# Revit family: Gleitlager T HV1, o.D., Ø20 bis Ø60mm (h=99mm bis 125mm)
name_source: partatom
category: HLS-Bauteile
revit_build: Autodesk Revit 2018 (Build: 20190510_1515(x64)
units: mm (PartAtom-declared; Revit-internal decimal feet)

## family parameters
Arbeitsebenenbasiert = Ja
Beim Laden mit Abzugskörper schneiden = Nein
Bemaßung runder Anschluss = Durchmesser verwenden
Gemeinsam genutzt = Ja
Immer vertikal = Nein
Klassifizierung = Keine
Raumberechnungspunkt = Nein
Teiletyp = Normal

## types (9) — shared parameters
Anzahl Rohrschellen = 2
Breite Schellenband = 35 mm
Breite Unterbau = 100 mm
Fabrikat = MEFA
Hersteller = MEFA
Kurztext1 = Gleitlager T 2 RS HV1 35x4
Länge Unterbau = 250 mm
Mengeneinheit = St
Schalldämmeinlage = ohne Dämmung
Sicherheitsfaktor = 1.54
Stärke Material = 8 mm  [stored 0.0262467 ft]
Stärke Schellenband = 4 mm
Verschluss = Mutter / Verschluss-Schraube
Vorgabe-Ansicht = 1219 mm
max. Höhe Unterbau = 125 mm
min. Höhe Unterbau = 100 mm
vpe = 1
zero-valued in all types: Dämmstärke

## per-type parameters (varying)
| type | Artikelnummer | EAN | Gewicht | Gewicht pro Bauteil | Kurztext2 | Schellenteil | max. Rohrachse | max. Rohraußendurchmesser | min. Rohrachse | min. Rohraußendurchmesser |
| Typ HV1, m. 2 RS, o.D., Ø20-22mm (h=99 bis 125mm) | 141afba0022 | 4250928460257 | 3.78 kg | 3.78 kg | 20 - 22 mm o. Dämm. 100x250 mm fsv | TL-141S_b0022 bis 0062, o.D : mit RS Ø20-22mm o.D | 136 mm | 22 mm  [stored 0.0721785 ft] | 109 mm | 20 mm  [stored 0.0656168 ft] |
| Typ HV1, m. 2 RS, o.D., Ø25mm (h=99 bis 125mm) | 141afba0025 | 4250928460264 | 3.80 kg | 3.80 kg | 25 mm o. Dämm. 100x250 mm fsv | TL-141S_b0022 bis 0062, o.D : mit RS Ø25mm o.D | 138 mm | 0 mm  [stored 0 ft] | 112 mm | 0 mm  [stored 0 ft] |
| Typ HV1, m. 2 RS, o.D., Ø27-28mm (h=99 bis 125mm) | 141afba0028 | 4250928460271 | 3.84 kg | 3.84 kg | 27 - 28 mm o. Dämm. 100x250 mm fsv | TL-141S_b0022 bis 0062, o.D : mit RS Ø27-28mm, o.D | 139 mm | 28 mm  [stored 0.0918635 ft] | 113 mm | 27 mm  [stored 0.0885827 ft] |
| Typ HV1, m. 2 RS, o.D., Ø32mm (h=99 bis 125mm) | 141afba0032 | 4250928460288 | 3.87 kg | 3.87 kg | 32 mm o. Dämm. 100x250 mm fsv | TL-141S_b0022 bis 0062, o.D : mit RS Ø32mm o.D | 141 mm | 0 mm  [stored 0 ft] | 115 mm | 0 mm  [stored 0 ft] |
| Typ HV1, m. 2 RS, o.D., Ø33-35mm (h=99 bis 125mm) | 141afba0035 | 4250928460295 | 3.89 kg | 3.89 kg | 33 - 35 mm o. Dämm. 100x250 mm fsv | TL-141S_b0022 bis 0062, o.D : mit RS Ø33-35mm o.D | 143 mm | 35 mm  [stored 0.114829 ft] | 116 mm | 33 mm |
| Typ HV1, m. 2 RS, o.D., Ø40-42mm (h=99 bis 125mm) | 141afba0042 | 4250928460301 | 3.95 kg | 3.95 kg | 40 - 42 mm o. Dämm. 100x250 mm fsv | TL-141S_b0022 bis 0062, o.D : mit RS Ø40-42mm o.D | 146 mm | 42 mm  [stored 0.137795 ft] | 119 mm | 40 mm  [stored 0.131234 ft] |
| Typ HV1, m. 2 RS, o.D., Ø48-50mm (h=99 bis 125mm) | 141afba0050 | 4250928460318 | 4.01 kg | 4.01 kg | 48 - 50 mm o. Dämm. 100x250 mm fsv | TL-141S_b0022 bis 0062, o.D : mit RS Ø48-50mm o.D | 150 mm | 50 mm  [stored 0.164042 ft] | 123 mm | 48 mm |
| Typ HV1, m. 2 RS, o.D., Ø54mm (h=99 bis 125mm) | 141afba0054 | 4250928460325 | 4.04 kg | 4.04 kg | 54 mm o. Dämm. 100x250 mm fsv | TL-141S_b0022 bis 0062, o.D : mit RS Ø54mm o.D | 152 mm | 0 mm  [stored 0 ft] | 126 mm | 0 mm  [stored 0 ft] |
| Typ HV1, m. 2 RS, o.D., Ø60mm (h=99 bis 125mm) | 141afba0060 | 4250928460332 | 4.12 kg | 4.12 kg | 60 mm o. Dämm. 100x250 mm fsv | TL-141S_b0022 bis 0062, o.D : mit RS Ø60mm o.D | 155 mm | 0 mm  [stored 0 ft] | 129 mm | 0 mm  [stored 0 ft] |

note: [stored X ft] marks values corroborated as IEEE doubles in the binary element streams (Revit-internal decimal feet)

## geometry (parser evidence)
native form markers: Sweep x8
no freeform markers — native parametric forms only
